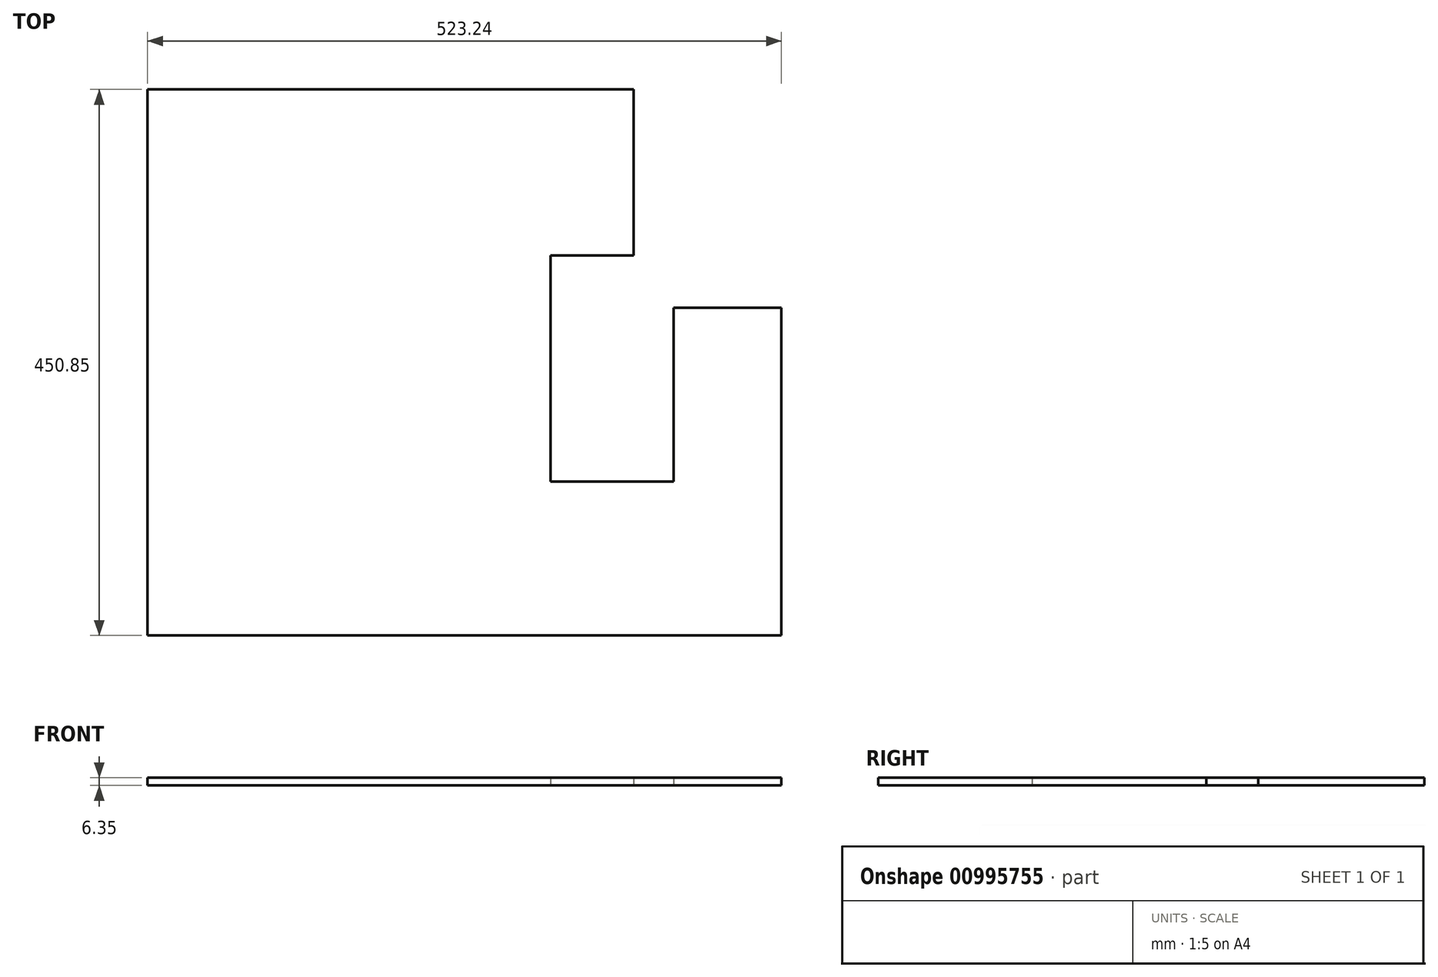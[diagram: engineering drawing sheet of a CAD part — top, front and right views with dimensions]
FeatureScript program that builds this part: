
annotation { "Feature Type Name" : "Feature", "Feature Type Description" : "" }
export const myFeature = defineFeature(function(context is Context, id is Id, definition is map)
    precondition{}
    {
        {
            var Q0;
            Q0=qCreatedBy(makeId("Top.planeOp"),FACE);
            var sketch = newSketch(context, id + "F0", { "sketchPlane" : qUnion([Q0])});
            skLineSegment(sketch, "E0", {"start": v(0, 0) * mm, "end": v(523.24, 0) * mm});
            skLineSegment(sketch, "E1", {"start": v(523.24, 0) * mm, "end": v(523.24, 270.75) * mm});
            skLineSegment(sketch, "E2", {"start": v(523.24, 270.75) * mm, "end": v(434.34, 270.75) * mm});
            skLineSegment(sketch, "E3", {"start": v(434.34, 270.75) * mm, "end": v(434.34, 127) * mm});
            skLineSegment(sketch, "E4", {"start": v(434.34, 127) * mm, "end": v(332.74, 127) * mm});
            skLineSegment(sketch, "E5", {"start": v(332.74, 127) * mm, "end": v(332.74, 313.7) * mm});
            skLineSegment(sketch, "E6", {"start": v(332.74, 313.7) * mm, "end": v(401.32, 313.7) * mm});
            skLineSegment(sketch, "E7", {"start": v(401.32, 313.7) * mm, "end": v(401.32, 450.85) * mm});
            skLineSegment(sketch, "E8", {"start": v(401.32, 450.85) * mm, "end": v(0, 450.85) * mm});
            skLineSegment(sketch, "E9", {"start": v(0, 450.85) * mm, "end": v(0, 0) * mm});
            skSolve(sketch);
        }
        {
            var Q0;
            Q0=makeQuery(id+"F0.imprint","IMPRINT",FACE,{"disambiguationData":[TD([[makeQuery(id+"F0.imprint","IMPRINT",EDGE,{"derivedFrom":sQuery(id+"F0.wireOp",EDGE,"E0")}),1.0]])]});
            extrude(context, id + "F1", {"entities" : qUnion([Q0]), "depth" : 6.35 * mm, "offsetDistance" : 25.4 * mm});
        }
    });
